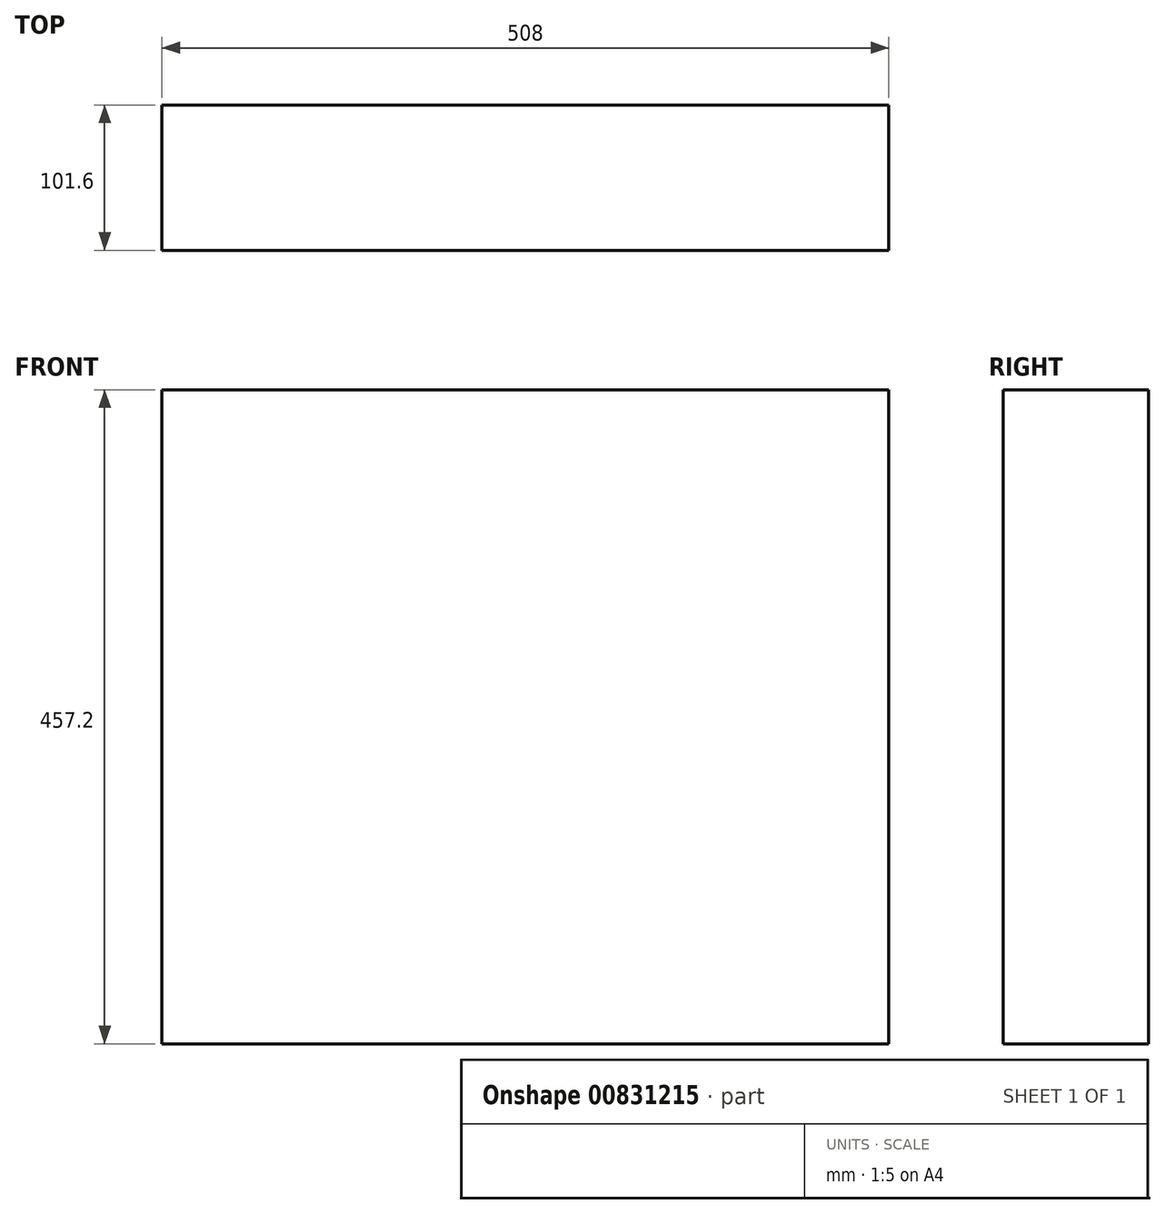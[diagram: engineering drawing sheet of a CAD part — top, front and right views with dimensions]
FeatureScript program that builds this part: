
annotation { "Feature Type Name" : "Feature", "Feature Type Description" : "" }
export const myFeature = defineFeature(function(context is Context, id is Id, definition is map)
    precondition{}
    {
        {
            var Q0;
            Q0=qCreatedBy(makeId("Front.planeOp"),FACE);
            var sketch = newSketch(context, id + "F0", { "sketchPlane" : qUnion([Q0])});
            skLineSegment(sketch, "E0.bottom", {"start": v(254, 228.6) * mm, "end": v(-254, 228.6) * mm});
            skLineSegment(sketch, "E0.top", {"start": v(254, -228.6) * mm, "end": v(-254, -228.6) * mm});
            skLineSegment(sketch, "E0.left", {"start": v(254, 228.6) * mm, "end": v(254, -228.6) * mm});
            skLineSegment(sketch, "E0.right", {"start": v(-254, 228.6) * mm, "end": v(-254, -228.6) * mm});
            skPoint(sketch, "E0.middle", {"position": v(0, 0) * mm});
            skSolve(sketch);
        }
        {
            var Q0;
            Q0=qSketchRegion(id+"F0",true);
            extrude(context, id + "F1", {"entities" : qUnion([Q0]), "depth" : 101.6 * mm, "offsetDistance" : 25.4 * mm});
        }
    });
